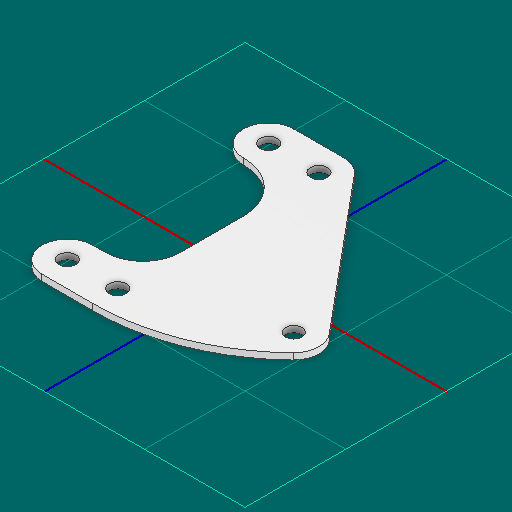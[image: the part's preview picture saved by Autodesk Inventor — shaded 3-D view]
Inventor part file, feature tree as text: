
AUTODESK INVENTOR PART (.ipt)
format: ipt  version: 2025 (Build 290162000, 162)  size: 141,312 bytes
history: native  units: in
note: dims shown in document units (in); Inventor stores cm internally (conversion verified against a paired STEP export)
features: other x5, sketch x1
ambient origin geometry x8: Origin, YZ Plane, XZ Plane, XY Plane, X Axis, Y Axis, Z Axis, Center Point
bodies: Solid1 (feature_tree)
feature tree (6):
  other  "gusset.ipt"
  other  "Blocks"
  other  "main"
  other  "Solid1::gusset.ipt"
  other  "TaggingFeature1"
  sketch  "Sketch1"  dims[d0=0.3937in d1=0.5in d2=0.375in]
